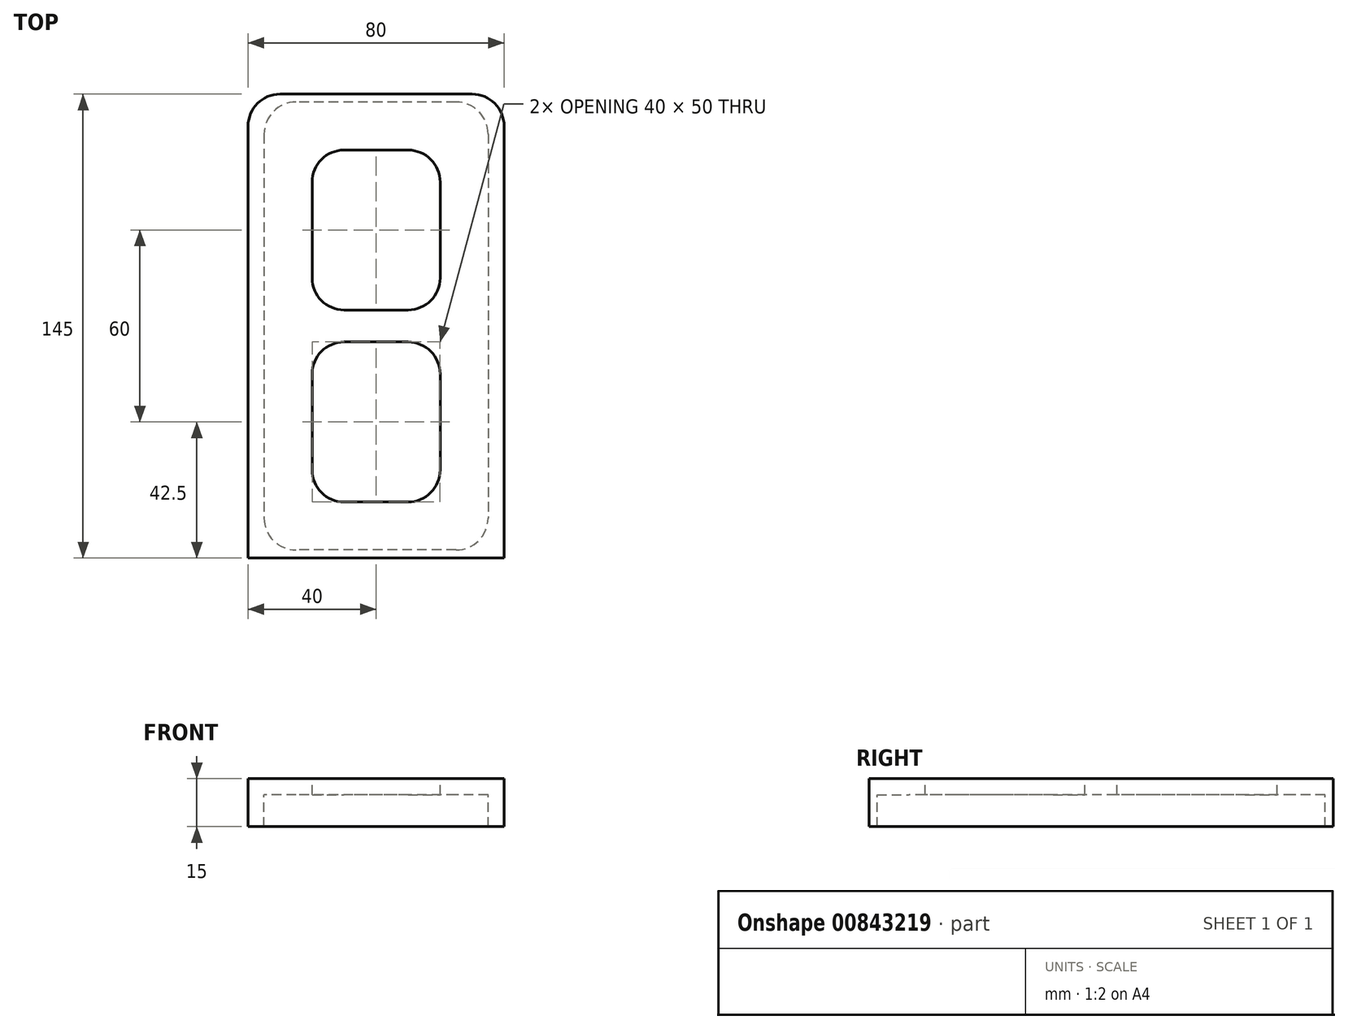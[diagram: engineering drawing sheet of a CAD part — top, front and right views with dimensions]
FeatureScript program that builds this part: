
annotation { "Feature Type Name" : "Feature", "Feature Type Description" : "" }
export const myFeature = defineFeature(function(context is Context, id is Id, definition is map)
    precondition{}
    {
        {
            var Q0;
            Q0=qCreatedBy(makeId("Top.planeOp"),FACE);
            var sketch = newSketch(context, id + "F0", { "sketchPlane" : qUnion([Q0])});
            skLineSegment(sketch, "E0.bottom", {"start": v(30, 72.5) * mm, "end": v(-30, 72.5) * mm});
            skLineSegment(sketch, "E0.top", {"start": v(40, -72.5) * mm, "end": v(-40, -72.5) * mm});
            skLineSegment(sketch, "E0.left", {"start": v(40, 62.5) * mm, "end": v(40, -72.5) * mm});
            skLineSegment(sketch, "E0.right", {"start": v(-40, 62.5) * mm, "end": v(-40, -72.5) * mm});
            skPoint(sketch, "E0.middle", {"position": v(0, 0) * mm});
            skLineSegment(sketch, "E1.bottom", {"start": v(25, 70) * mm, "end": v(-25, 70) * mm});
            skLineSegment(sketch, "E1.top", {"start": v(25, -70) * mm, "end": v(-25, -70) * mm});
            skLineSegment(sketch, "E1.left", {"start": v(35, 60) * mm, "end": v(35, -60) * mm});
            skLineSegment(sketch, "E1.right", {"start": v(-35, 60) * mm, "end": v(-35, -60) * mm});
            skPoint(sketch, "E2.visualSharp", {"position": v(-35, 70) * mm});
            skArc(sketch, "E2.filletArc", {"start": v(-25, 70) * mm, "mid": v(-32.07, 67.07) * mm, "end": v(-35, 60) * mm});
            skPoint(sketch, "E3.visualSharp", {"position": v(-40, 72.5) * mm});
            skArc(sketch, "E3.filletArc", {"start": v(-30, 72.5) * mm, "mid": v(-37.07, 69.57) * mm, "end": v(-40, 62.5) * mm});
            skPoint(sketch, "E4.visualSharp", {"position": v(35, 70) * mm});
            skArc(sketch, "E4.filletArc", {"start": v(35, 60) * mm, "mid": v(32.07, 67.07) * mm, "end": v(25, 70) * mm});
            skPoint(sketch, "E5.visualSharp", {"position": v(40, 72.5) * mm});
            skArc(sketch, "E5.filletArc", {"start": v(40, 62.5) * mm, "mid": v(37.07, 69.57) * mm, "end": v(30, 72.5) * mm});
            skPoint(sketch, "E6.visualSharp", {"position": v(-35, -70) * mm});
            skArc(sketch, "E6.filletArc", {"start": v(-35, -60) * mm, "mid": v(-32.07, -67.07) * mm, "end": v(-25, -70) * mm});
            skPoint(sketch, "E7.visualSharp", {"position": v(35, -70) * mm});
            skArc(sketch, "E7.filletArc", {"start": v(25, -70) * mm, "mid": v(32.07, -67.07) * mm, "end": v(35, -60) * mm});
            skLineSegment(sketch, "E8.bottom", {"start": v(10, 55) * mm, "end": v(-10, 55) * mm});
            skLineSegment(sketch, "E8.top", {"start": v(10, -55) * mm, "end": v(-10, -55) * mm});
            skPoint(sketch, "E9.visualSharp", {"position": v(-20, 55) * mm});
            skArc(sketch, "E9.filletArc", {"start": v(-10, 55) * mm, "mid": v(-17.07, 52.07) * mm, "end": v(-20, 45) * mm});
            skPoint(sketch, "E10.visualSharp", {"position": v(20, 55) * mm});
            skArc(sketch, "E10.filletArc", {"start": v(20, 45) * mm, "mid": v(17.07, 52.07) * mm, "end": v(10, 55) * mm});
            skPoint(sketch, "E11.visualSharp", {"position": v(-20, -55) * mm});
            skArc(sketch, "E11.filletArc", {"start": v(-20, -45) * mm, "mid": v(-17.07, -52.07) * mm, "end": v(-10, -55) * mm});
            skPoint(sketch, "E12.visualSharp", {"position": v(20, -55) * mm});
            skArc(sketch, "E12.filletArc", {"start": v(10, -55) * mm, "mid": v(17.07, -52.07) * mm, "end": v(20, -45) * mm});
            skLineSegment(sketch, "E13", {"start": v(-20, -15) * mm, "end": v(-20, -45) * mm});
            skLineSegment(sketch, "E14", {"start": v(-10, -5) * mm, "end": v(10, -5) * mm});
            skLineSegment(sketch, "E15", {"start": v(20, -15) * mm, "end": v(20, -45) * mm});
            skLineSegment(sketch, "E16", {"start": v(-20, 45) * mm, "end": v(-20, 15) * mm});
            skLineSegment(sketch, "E17", {"start": v(-10, 5) * mm, "end": v(10, 5) * mm});
            skLineSegment(sketch, "E18", {"start": v(20, 15) * mm, "end": v(20, 45) * mm});
            skPoint(sketch, "E19.visualSharp", {"position": v(-20, -5) * mm});
            skArc(sketch, "E19.filletArc", {"start": v(-10, -5) * mm, "mid": v(-17.07, -7.93) * mm, "end": v(-20, -15) * mm});
            skPoint(sketch, "E20.visualSharp", {"position": v(20, -5) * mm});
            skArc(sketch, "E20.filletArc", {"start": v(20, -15) * mm, "mid": v(17.07, -7.93) * mm, "end": v(10, -5) * mm});
            skPoint(sketch, "E21.visualSharp", {"position": v(20, 5) * mm});
            skArc(sketch, "E21.filletArc", {"start": v(10, 5) * mm, "mid": v(17.07, 7.93) * mm, "end": v(20, 15) * mm});
            skPoint(sketch, "E22.visualSharp", {"position": v(-20, 5) * mm});
            skArc(sketch, "E22.filletArc", {"start": v(-20, 15) * mm, "mid": v(-17.07, 7.93) * mm, "end": v(-10, 5) * mm});
            skSolve(sketch);
        }
        {
            var Q0;
            Q0=makeQuery(id+"F0.imprint","IMPRINT",FACE,{"disambiguationData":[TD([[makeQuery(id+"F0.imprint","IMPRINT",EDGE,{"derivedFrom":sQuery(id+"F0.wireOp",EDGE,"E0.bottom")}),1.0]])]});
            var Q1;
            Q1=makeQuery(id+"F0.imprint","IMPRINT",FACE,{"disambiguationData":[TD([[makeQuery(id+"F0.imprint","IMPRINT",EDGE,{"derivedFrom":sQuery(id+"F0.wireOp",EDGE,"E1.bottom")}),1.0]])]});
            extrude(context, id + "F1", {"entities" : qUnion([Q0, Q1]), "oppositeDirection" : true, "depth" : 5 * mm, "offsetDistance" : 25 * mm});
        }
        {
            var Q0;
            Q0=makeQuery(id+"F0.imprint","IMPRINT",FACE,{"disambiguationData":[TD([[makeQuery(id+"F0.imprint","IMPRINT",EDGE,{"derivedFrom":sQuery(id+"F0.wireOp",EDGE,"E0.bottom")}),1.0]])]});
            extrude(context, id + "F2", {"entities" : qUnion([Q0]), "operationType" : NewBodyOperationType.ADD, "oppositeDirection" : true, "depth" : 15 * mm, "offsetDistance" : 25 * mm});
        }
    });
